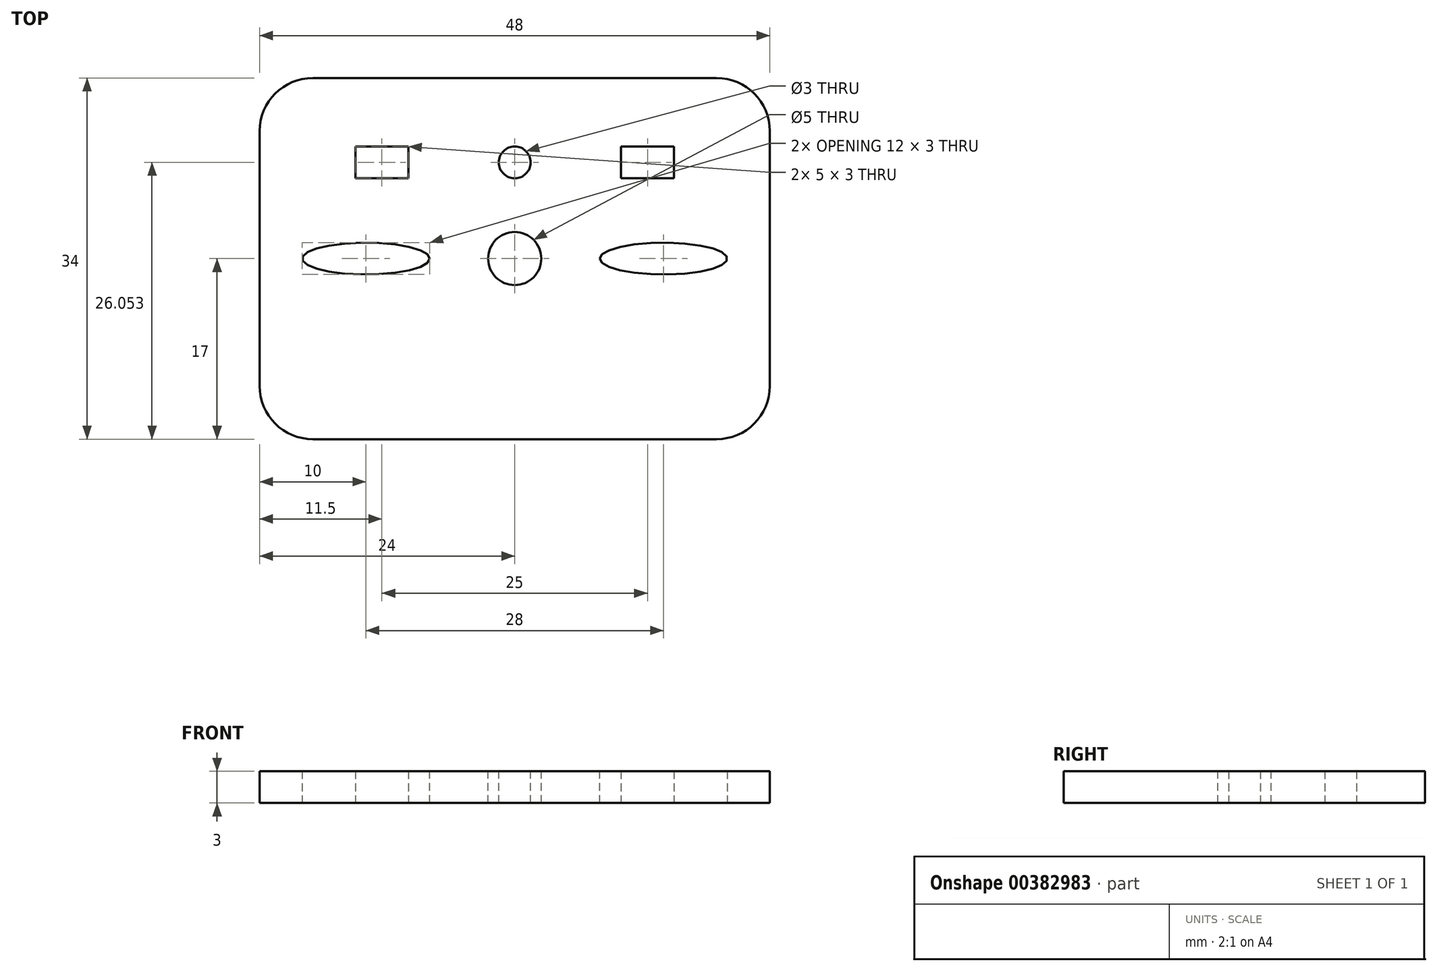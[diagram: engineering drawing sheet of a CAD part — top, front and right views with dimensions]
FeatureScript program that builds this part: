
annotation { "Feature Type Name" : "Feature", "Feature Type Description" : "" }
export const myFeature = defineFeature(function(context is Context, id is Id, definition is map)
    precondition{}
    {
        {
            var Q0;
            Q0=qCreatedBy(makeId("Top.planeOp"),FACE);
            var sketch = newSketch(context, id + "F0", { "sketchPlane" : qUnion([Q0])});
            skLineSegment(sketch, "E0.bottom", {"start": v(24, 17) * mm, "end": v(-24, 17) * mm});
            skLineSegment(sketch, "E0.top", {"start": v(24, -17) * mm, "end": v(-24, -17) * mm});
            skLineSegment(sketch, "E0.left", {"start": v(24, 17) * mm, "end": v(24, -17) * mm});
            skLineSegment(sketch, "E0.right", {"start": v(-24, 17) * mm, "end": v(-24, -17) * mm});
            skPoint(sketch, "E0.middle", {"position": v(0, 0) * mm});
            skLineSegment(sketch, "E1.bottom", {"start": v(15, 7.55) * mm, "end": v(10, 7.55) * mm});
            skLineSegment(sketch, "E1.top", {"start": v(15, 10.55) * mm, "end": v(10, 10.55) * mm});
            skLineSegment(sketch, "E1.left", {"start": v(15, 7.55) * mm, "end": v(15, 10.55) * mm});
            skLineSegment(sketch, "E1.right", {"start": v(10, 7.55) * mm, "end": v(10, 10.55) * mm});
            skPoint(sketch, "E1.middle", {"position": v(12.5, 9.05) * mm});
            skLineSegment(sketch, "E2.bottom", {"start": v(-10, 7.55) * mm, "end": v(-15, 7.55) * mm});
            skLineSegment(sketch, "E2.top", {"start": v(-10, 10.55) * mm, "end": v(-15, 10.55) * mm});
            skLineSegment(sketch, "E2.left", {"start": v(-10, 7.55) * mm, "end": v(-10, 10.55) * mm});
            skLineSegment(sketch, "E2.right", {"start": v(-15, 7.55) * mm, "end": v(-15, 10.55) * mm});
            skPoint(sketch, "E2.middle", {"position": v(-12.5, 9.05) * mm});
            skSolve(sketch);
        }
        {
            var Q0;
            Q0=makeQuery(id+"F0.imprint","IMPRINT",FACE,{"disambiguationData":[TD([[makeQuery(id+"F0.imprint","IMPRINT",EDGE,{"derivedFrom":sQuery(id+"F0.wireOp",EDGE,"E0.bottom")}),1.0]])]});
            extrude(context, id + "F1", {"entities" : qUnion([Q0]), "depth" : 3 * mm});
        }
        {
            var Q0;
            Q0=makeQuery(id+"F1.opExtrude","CAP_FACE",FACE,{"disambiguationData":[OSD([sQuery(id+"F0.wireOp",EDGE,"E0.bottom"),sQuery(id+"F0.wireOp",EDGE,"E0.top"),sQuery(id+"F0.wireOp",EDGE,"E0.left"),sQuery(id+"F0.wireOp",EDGE,"E0.right"),sQuery(id+"F0.wireOp",EDGE,"E1.bottom"),sQuery(id+"F0.wireOp",EDGE,"E1.top"),sQuery(id+"F0.wireOp",EDGE,"E1.left"),sQuery(id+"F0.wireOp",EDGE,"E1.right"),sQuery(id+"F0.wireOp",EDGE,"E2.bottom"),sQuery(id+"F0.wireOp",EDGE,"E2.top"),sQuery(id+"F0.wireOp",EDGE,"E2.left"),sQuery(id+"F0.wireOp",EDGE,"E2.right")])],"isStart":false});
            var sketch = newSketch(context, id + "F2", { "sketchPlane" : qUnion([Q0])});
            skEllipse(sketch, "E3", {"center": v(-14, 0) * mm, "majorRadius": 6 * mm, "minorRadius": 1.5 * mm, "majorAxis": v(1, 0)});
            skEllipse(sketch, "E4.MirrorC", {"center": v(14, 0) * mm, "majorRadius": 6 * mm, "minorRadius": 1.5 * mm, "majorAxis": v(-1, 0)});
            skSolve(sketch);
        }
        {
            var Q0;
            Q0 = qSketchRegion(id + "F2", true);
            extrude(context, id + "F3", {"entities" : qUnion([Q0]), "operationType" : NewBodyOperationType.REMOVE, "oppositeDirection" : true, "depth" : 25 * mm});
        }
        {
            var Q0;
            Q0=makeQuery(id+"F1.opExtrude","CAP_FACE",FACE,{"disambiguationData":[OSD([sQuery(id+"F0.wireOp",EDGE,"E0.bottom"),sQuery(id+"F0.wireOp",EDGE,"E0.top"),sQuery(id+"F0.wireOp",EDGE,"E0.left"),sQuery(id+"F0.wireOp",EDGE,"E0.right"),sQuery(id+"F0.wireOp",EDGE,"E1.bottom"),sQuery(id+"F0.wireOp",EDGE,"E1.top"),sQuery(id+"F0.wireOp",EDGE,"E1.left"),sQuery(id+"F0.wireOp",EDGE,"E1.right"),sQuery(id+"F0.wireOp",EDGE,"E2.bottom"),sQuery(id+"F0.wireOp",EDGE,"E2.top"),sQuery(id+"F0.wireOp",EDGE,"E2.left"),sQuery(id+"F0.wireOp",EDGE,"E2.right")])],"isStart":false});
            var sketch = newSketch(context, id + "F4", { "sketchPlane" : qUnion([Q0])});
            skCircle(sketch, "E5", {"center": v(0, 9.05) * mm, "radius": 1.5 * mm});
            skSolve(sketch);
        }
        {
            var Q0;
            Q0 = qSketchRegion(id + "F4", true);
            extrude(context, id + "F5", {"entities" : qUnion([Q0]), "operationType" : NewBodyOperationType.REMOVE, "oppositeDirection" : true, "depth" : 25 * mm});
        }
        {
            var Q0;
            Q0=makeQuery(id+"F1.opExtrude","CAP_FACE",FACE,{"disambiguationData":[OSD([sQuery(id+"F0.wireOp",EDGE,"E0.bottom"),sQuery(id+"F0.wireOp",EDGE,"E0.top"),sQuery(id+"F0.wireOp",EDGE,"E0.left"),sQuery(id+"F0.wireOp",EDGE,"E0.right"),sQuery(id+"F0.wireOp",EDGE,"E1.bottom"),sQuery(id+"F0.wireOp",EDGE,"E1.top"),sQuery(id+"F0.wireOp",EDGE,"E1.left"),sQuery(id+"F0.wireOp",EDGE,"E1.right"),sQuery(id+"F0.wireOp",EDGE,"E2.bottom"),sQuery(id+"F0.wireOp",EDGE,"E2.top"),sQuery(id+"F0.wireOp",EDGE,"E2.left"),sQuery(id+"F0.wireOp",EDGE,"E2.right")])],"isStart":false});
            var sketch = newSketch(context, id + "F6", { "sketchPlane" : qUnion([Q0])});
            skCircle(sketch, "E6", {"center": v(0, 0) * mm, "radius": 2.5 * mm});
            skSolve(sketch);
        }
        {
            var Q0;
            Q0 = qSketchRegion(id + "F6", true);
            extrude(context, id + "F7", {"entities" : qUnion([Q0]), "operationType" : NewBodyOperationType.REMOVE, "oppositeDirection" : true, "depth" : 25 * mm});
        }
        {
            var Q0;
            Q0=makeQuery(id+"F1.opExtrude","SWEPT_EDGE",EDGE,{"disambiguationData":[OSD([sQuery(id+"F0.wireOp",EDGE,"E0.bottom"),sQuery(id+"F0.wireOp",EDGE,"E0.right")])]});
            var Q1;
            Q1=makeQuery(id+"F1.opExtrude","SWEPT_EDGE",EDGE,{"disambiguationData":[OSD([sQuery(id+"F0.wireOp",EDGE,"E0.bottom"),sQuery(id+"F0.wireOp",EDGE,"E0.left")])]});
            var Q2;
            Q2=makeQuery(id+"F1.opExtrude","SWEPT_EDGE",EDGE,{"disambiguationData":[OSD([sQuery(id+"F0.wireOp",EDGE,"E0.top"),sQuery(id+"F0.wireOp",EDGE,"E0.left")])]});
            var Q3;
            Q3=makeQuery(id+"F1.opExtrude","SWEPT_EDGE",EDGE,{"disambiguationData":[OSD([sQuery(id+"F0.wireOp",EDGE,"E0.top"),sQuery(id+"F0.wireOp",EDGE,"E0.right")])]});
            fillet(context, id + "F8", {"entities" : qUnion([Q0, Q1, Q2, Q3]), "radius" : 5 * mm, "tangentPropagation" : true, "allowEdgeOverflow" : false});
        }
    });
